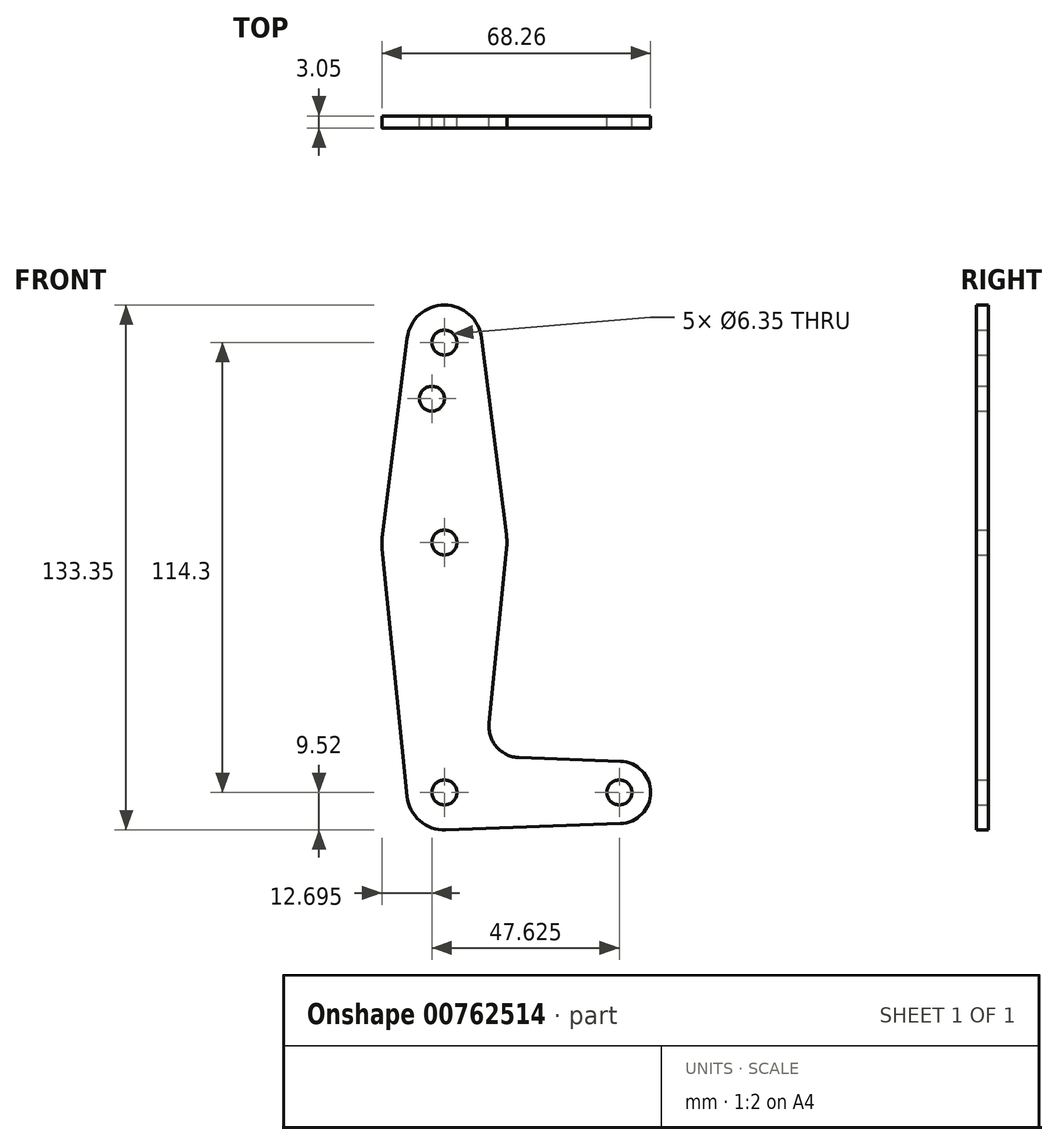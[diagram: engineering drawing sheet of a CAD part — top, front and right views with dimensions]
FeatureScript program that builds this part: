
annotation { "Feature Type Name" : "Feature", "Feature Type Description" : "" }
export const myFeature = defineFeature(function(context is Context, id is Id, definition is map)
    precondition{}
    {
        {
            var Q0;
            Q0=qCreatedBy(makeId("Front.planeOp"),FACE);
            var sketch = newSketch(context, id + "F0", { "sketchPlane" : qUnion([Q0])});
            skLineSegment(sketch, "E0", {"start": v(0, 0) * mm, "end": v(0, 114.3) * mm, "construction": true});
            skLineSegment(sketch, "E1", {"start": v(0, 0) * mm, "end": v(44.45, 0) * mm, "construction": true});
            skCircle(sketch, "E2", {"center": v(0, 114.3) * mm, "radius": 9.53 * mm});
            skCircle(sketch, "E3", {"center": v(0, 0) * mm, "radius": 9.53 * mm});
            skCircle(sketch, "E4", {"center": v(0, 63.5) * mm, "radius": 15.88 * mm});
            skCircle(sketch, "E5", {"center": v(44.45, 0) * mm, "radius": 7.94 * mm});
            skLineSegment(sketch, "E6", {"start": v(-9.45, 115.5) * mm, "end": v(-15.75, 65.48) * mm});
            skLineSegment(sketch, "E7", {"start": v(-15.8, 61.91) * mm, "end": v(-9.48, -0.95) * mm});
            skLineSegment(sketch, "E8", {"start": v(11.34, 17.6) * mm, "end": v(15.8, 61.91) * mm});
            skLineSegment(sketch, "E9", {"start": v(9.45, 115.5) * mm, "end": v(15.75, 65.48) * mm});
            skLineSegment(sketch, "E10", {"start": v(18.97, 8.85) * mm, "end": v(44.73, 7.93) * mm});
            skLineSegment(sketch, "E11", {"start": v(0.34, -9.52) * mm, "end": v(44.73, -7.93) * mm});
            skCircle(sketch, "E12", {"center": v(0, 114.3) * mm, "radius": 3.18 * mm});
            skCircle(sketch, "E13", {"center": v(-3.18, 100.03) * mm, "radius": 3.18 * mm});
            skCircle(sketch, "E14", {"center": v(0, 63.5) * mm, "radius": 3.18 * mm});
            skCircle(sketch, "E15", {"center": v(0, 0) * mm, "radius": 3.18 * mm});
            skCircle(sketch, "E16", {"center": v(44.45, 0) * mm, "radius": 3.18 * mm});
            skArc(sketch, "E17.filletArc", {"start": v(11.34, 17.6) * mm, "mid": v(13.26, 11.57) * mm, "end": v(18.97, 8.85) * mm});
            skSolve(sketch);
        }
        {
            var Q0;
            Q0=makeQuery(id+"F0.imprint","IMPRINT",FACE,{"disambiguationData":[TD([[makeQuery(id+"F0.imprint","IMPRINT",EDGE,{"derivedFrom":sQuery(id+"F0.wireOp",EDGE,"E12")}),-1.0]])]});
            var Q1;
            {var subQ1=sQuery(id+"F0.wireOp",EDGE,"E6");Q1=makeQuery(id+"F0.imprint","IMPRINT",FACE,{"disambiguationData":[TD([[makeQuery(id+"F0.imprint","IMPRINT",EDGE,{"derivedFrom":subQ1}),1.0]])]});}
            var Q2;
            Q2=makeQuery(id+"F0.imprint","IMPRINT",FACE,{"disambiguationData":[TD([[makeQuery(id+"F0.imprint","IMPRINT",EDGE,{"derivedFrom":sQuery(id+"F0.wireOp",EDGE,"E14")}),-1.0]])]});
            var Q3;
            {var subQ0=sQuery(id+"F0.wireOp",EDGE,"E7");Q3=makeQuery(id+"F0.imprint","IMPRINT",FACE,{"disambiguationData":[TD([[makeQuery(id+"F0.imprint","IMPRINT",EDGE,{"derivedFrom":subQ0}),1.0]])]});}
            var Q4;
            Q4=makeQuery(id+"F0.imprint","IMPRINT",FACE,{"disambiguationData":[TD([[makeQuery(id+"F0.imprint","IMPRINT",EDGE,{"derivedFrom":sQuery(id+"F0.wireOp",EDGE,"E15")}),-1.0]])]});
            var Q5;
            Q5=makeQuery(id+"F0.imprint","IMPRINT",FACE,{"disambiguationData":[TD([[makeQuery(id+"F0.imprint","IMPRINT",EDGE,{"derivedFrom":sQuery(id+"F0.wireOp",EDGE,"E16")}),-1.0]])]});
            extrude(context, id + "F1", {"entities" : qUnion([Q0, Q1, Q2, Q3, Q4, Q5]), "depth" : 3.05 * mm, "offsetDistance" : 25.4 * mm});
        }
    });
